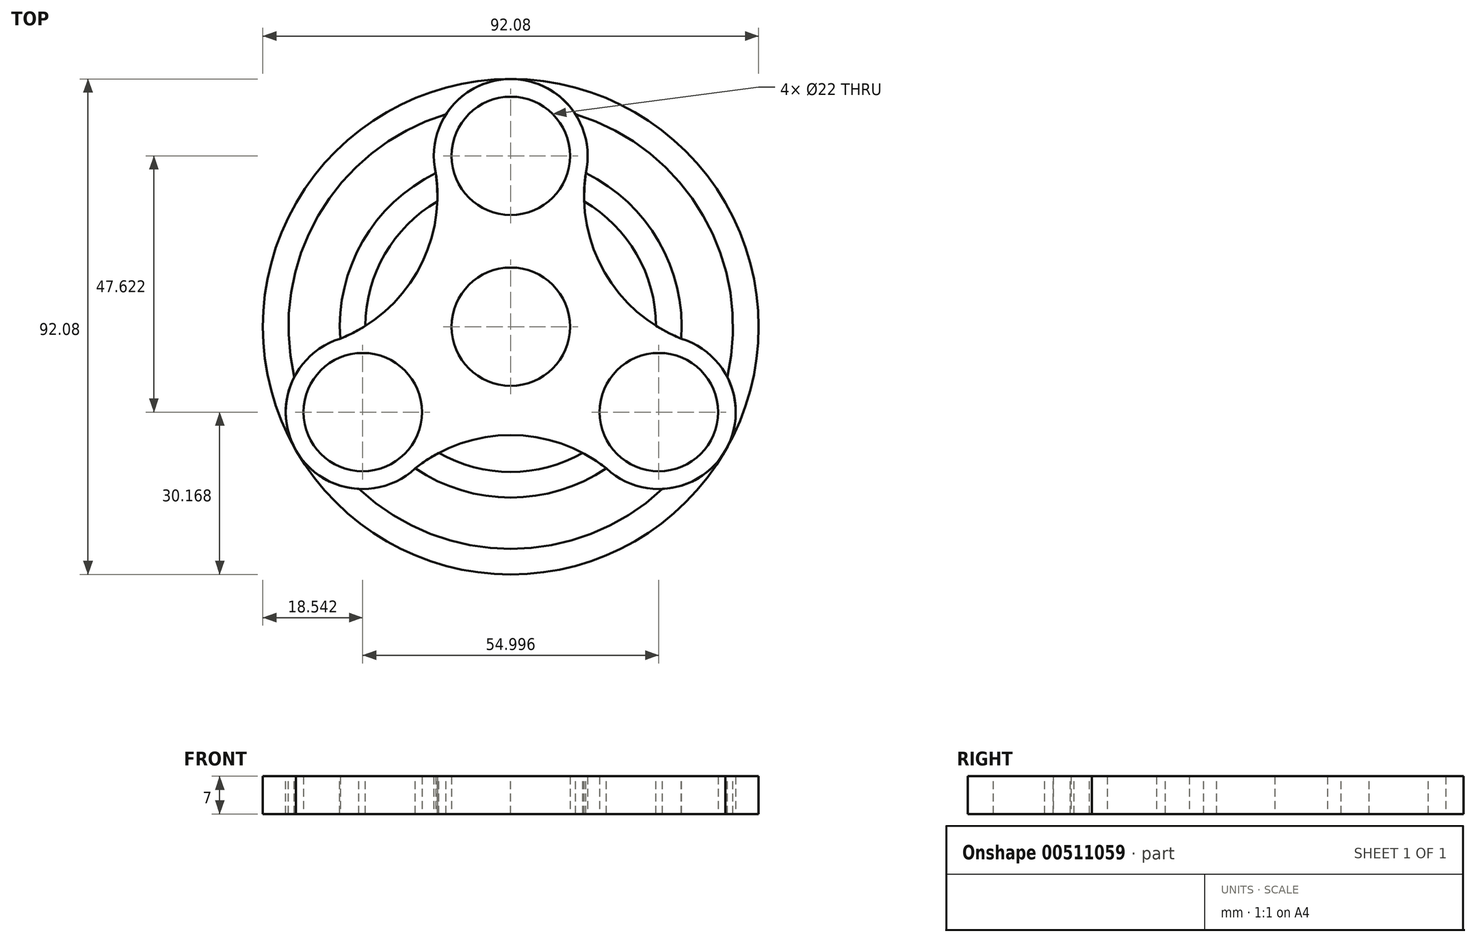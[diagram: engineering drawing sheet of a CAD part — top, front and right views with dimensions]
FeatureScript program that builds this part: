
annotation { "Feature Type Name" : "Feature", "Feature Type Description" : "" }
export const myFeature = defineFeature(function(context is Context, id is Id, definition is map)
    precondition{}
    {
        {
            var Q0;
            Q0=qCreatedBy(makeId("Top.planeOp"),FACE);
            var sketch = newSketch(context, id + "F0", { "sketchPlane" : qUnion([Q0])});
            skArc(sketch, "E0", {"start": v(-31.67, -2.2) * mm, "mid": v(-27.5, -15.87) * mm, "end": v(-17.75, -26.32) * mm});
            skCircle(sketch, "E1", {"center": v(0, 31.75) * mm, "radius": 14.29 * mm});
            skCircle(sketch, "E2", {"center": v(27.5, -15.87) * mm, "radius": 14.29 * mm});
            skCircle(sketch, "E3", {"center": v(-27.5, -15.87) * mm, "radius": 14.29 * mm});
            skArc(sketch, "E4", {"start": v(-31.67, -2.2) * mm, "mid": v(-17.44, 10.07) * mm, "end": v(-13.92, 28.54) * mm});
            skArc(sketch, "E5", {"start": v(13.92, 28.54) * mm, "mid": v(17.44, 10.07) * mm, "end": v(31.67, -2.2) * mm});
            skArc(sketch, "E6", {"start": v(17.75, -26.32) * mm, "mid": v(0, -20.14) * mm, "end": v(-17.75, -26.32) * mm});
            skArc(sketch, "E7.trimOffspring", {"start": v(13.92, 28.54) * mm, "mid": v(0, 31.75) * mm, "end": v(-13.92, 28.54) * mm});
            skArc(sketch, "E8.trimOffspring", {"start": v(17.75, -26.32) * mm, "mid": v(27.5, -15.87) * mm, "end": v(31.67, -2.2) * mm});
            skCircle(sketch, "E9", {"center": v(0, 31.75) * mm, "radius": 11 * mm});
            skCircle(sketch, "E10", {"center": v(-27.5, -15.87) * mm, "radius": 11 * mm});
            skCircle(sketch, "E11", {"center": v(27.5, -15.87) * mm, "radius": 11 * mm});
            skCircle(sketch, "E12", {"center": v(0, 0) * mm, "radius": 11 * mm});
            skSolve(sketch);
        }
        {
            var Q0;
            {var subQ0=sQuery(id+"F0.wireOp",EDGE,"E7.trimOffspring");var subQ4=sQuery(id+"F0.wireOp",EDGE,"E9");var subQ6=makeQuery(id+"F0.imprint","INTERSECT",VERTEX,{"disambiguationData":[OD(0.0)],"derivedFrom":[subQ0,subQ4]});Q0=makeQuery(id+"F0.imprint","IMPRINT",FACE,{"disambiguationData":[TD([[makeQuery(id+"F0.imprint","IMPRINT",EDGE,{"disambiguationData":[TD([[subQ6,-1.0]])],"derivedFrom":subQ4}),-1.0]])]});}
            var Q1;
            {var subQ0=sQuery(id+"F0.wireOp",EDGE,"E7.trimOffspring");var subQ4=sQuery(id+"F0.wireOp",EDGE,"E9");var subQ5=makeQuery(id+"F0.imprint","INTERSECT",VERTEX,{"disambiguationData":[OD(0.0)],"derivedFrom":[subQ0,subQ4]});Q1=makeQuery(id+"F0.imprint","IMPRINT",FACE,{"disambiguationData":[TD([[makeQuery(id+"F0.imprint","IMPRINT",EDGE,{"disambiguationData":[TD([[subQ5,1.0]])],"derivedFrom":subQ4}),-1.0]])]});}
            var Q2;
            {var subQ0=sQuery(id+"F0.wireOp",EDGE,"E4");Q2=makeQuery(id+"F0.imprint","IMPRINT",FACE,{"disambiguationData":[TD([[makeQuery(id+"F0.imprint","IMPRINT",EDGE,{"derivedFrom":subQ0}),-1.0]])]});}
            var Q3;
            {var subQ0=sQuery(id+"F0.wireOp",EDGE,"E8.trimOffspring");var subQ4=sQuery(id+"F0.wireOp",EDGE,"E11");var subQ5=makeQuery(id+"F0.imprint","INTERSECT",VERTEX,{"disambiguationData":[OD(0.0)],"derivedFrom":[subQ0,subQ4]});Q3=makeQuery(id+"F0.imprint","IMPRINT",FACE,{"disambiguationData":[TD([[makeQuery(id+"F0.imprint","IMPRINT",EDGE,{"disambiguationData":[TD([[subQ5,1.0]])],"derivedFrom":subQ4}),-1.0]])]});}
            var Q4;
            {var subQ0=sQuery(id+"F0.wireOp",EDGE,"E8.trimOffspring");var subQ4=sQuery(id+"F0.wireOp",EDGE,"E11");var subQ5=makeQuery(id+"F0.imprint","INTERSECT",VERTEX,{"disambiguationData":[OD(0.0)],"derivedFrom":[subQ0,subQ4]});Q4=makeQuery(id+"F0.imprint","IMPRINT",FACE,{"disambiguationData":[TD([[makeQuery(id+"F0.imprint","IMPRINT",EDGE,{"disambiguationData":[TD([[subQ5,-1.0]])],"derivedFrom":subQ4}),-1.0]])]});}
            var Q5;
            {var subQ1=sQuery(id+"F0.wireOp",EDGE,"E0");var subQ3=sQuery(id+"F0.wireOp",EDGE,"E10");var subQ4=makeQuery(id+"F0.imprint","INTERSECT",VERTEX,{"disambiguationData":[OD(0.0)],"derivedFrom":[subQ1,subQ3]});Q5=makeQuery(id+"F0.imprint","IMPRINT",FACE,{"disambiguationData":[TD([[makeQuery(id+"F0.imprint","IMPRINT",EDGE,{"disambiguationData":[TD([[subQ4,1.0]])],"derivedFrom":subQ3}),-1.0]])]});}
            var Q6;
            {var subQ1=sQuery(id+"F0.wireOp",EDGE,"E0");var subQ3=sQuery(id+"F0.wireOp",EDGE,"E10");var subQ4=makeQuery(id+"F0.imprint","INTERSECT",VERTEX,{"disambiguationData":[OD(0.0)],"derivedFrom":[subQ1,subQ3]});Q6=makeQuery(id+"F0.imprint","IMPRINT",FACE,{"disambiguationData":[TD([[makeQuery(id+"F0.imprint","IMPRINT",EDGE,{"disambiguationData":[TD([[subQ4,-1.0]])],"derivedFrom":subQ3}),-1.0]])]});}
            extrude(context, id + "F1", {"entities" : qUnion([Q0, Q1, Q2, Q3, Q4, Q5, Q6]), "depth" : 7 * mm});
        }
        {
            var Q0;
            Q0=makeQuery(id+"F1.opExtrude","CAP_FACE",FACE,{"disambiguationData":[OSD([sQuery(id+"F0.wireOp",EDGE,"E1"),sQuery(id+"F0.wireOp",EDGE,"E2"),sQuery(id+"F0.wireOp",EDGE,"E3"),sQuery(id+"F0.wireOp",EDGE,"E4"),sQuery(id+"F0.wireOp",EDGE,"E5"),sQuery(id+"F0.wireOp",EDGE,"E6"),sQuery(id+"F0.wireOp",EDGE,"E9"),sQuery(id+"F0.wireOp",EDGE,"E10"),sQuery(id+"F0.wireOp",EDGE,"E11"),sQuery(id+"F0.wireOp",EDGE,"E12")])],"isStart":false});
            var sketch = newSketch(context, id + "F2", { "sketchPlane" : qUnion([Q0])});
            skCircle(sketch, "E13", {"center": v(0, 0) * mm, "radius": 46.04 * mm});
            skArc(sketch, "E14", {"start": v(-12, 39.49) * mm, "mid": v(-35.74, 20.64) * mm, "end": v(-40.2, -9.34) * mm});
            skArc(sketch, "E15", {"start": v(-13.63, 23.29) * mm, "mid": v(-23.37, 13.5) * mm, "end": v(-26.99, 0.17) * mm});
            skArc(sketch, "E16.0", {"start": v(13.92, 28.54) * mm, "mid": v(0, 46.04) * mm, "end": v(-13.92, 28.54) * mm});
            skArc(sketch, "E17.0", {"start": v(-31.67, -2.2) * mm, "mid": v(-17.44, 10.07) * mm, "end": v(-13.92, 28.54) * mm});
            skArc(sketch, "E18.0", {"start": v(13.92, 28.54) * mm, "mid": v(17.44, 10.07) * mm, "end": v(31.67, -2.2) * mm});
            skArc(sketch, "E19.0", {"start": v(17.75, -26.32) * mm, "mid": v(39.87, -23.01) * mm, "end": v(31.67, -2.2) * mm});
            skArc(sketch, "E20.0", {"start": v(17.75, -26.32) * mm, "mid": v(0, -20.14) * mm, "end": v(-17.75, -26.32) * mm});
            skArc(sketch, "E21.0", {"start": v(-31.67, -2.2) * mm, "mid": v(-39.87, -23.01) * mm, "end": v(-17.75, -26.32) * mm});
            skArc(sketch, "E22.trimOffspring", {"start": v(26.99, 0.17) * mm, "mid": v(23.37, 13.5) * mm, "end": v(13.63, 23.29) * mm});
            skArc(sketch, "E23.trimOffspring", {"start": v(-13.36, -23.45) * mm, "mid": v(0, -26.99) * mm, "end": v(13.36, -23.45) * mm});
            skArc(sketch, "E24.trimOffspring", {"start": v(-28.2, -30.14) * mm, "mid": v(0, -41.28) * mm, "end": v(28.2, -30.14) * mm});
            skArc(sketch, "E25.trimOffspring", {"start": v(40.2, -9.34) * mm, "mid": v(35.74, 20.64) * mm, "end": v(12, 39.49) * mm});
            skArc(sketch, "E26", {"start": v(-13.92, 28.54) * mm, "mid": v(-27.5, 15.88) * mm, "end": v(-31.67, -2.2) * mm});
            skArc(sketch, "E27.trimOffspring", {"start": v(31.67, -2.2) * mm, "mid": v(27.5, 15.88) * mm, "end": v(13.92, 28.54) * mm});
            skArc(sketch, "E28.trimOffspring", {"start": v(-17.75, -26.32) * mm, "mid": v(0, -31.75) * mm, "end": v(17.75, -26.32) * mm});
            skSolve(sketch);
        }
        {
            var Q0;
            {var subQ5=sQuery(id+"F2.wireOp",EDGE,"E14");Q0=makeQuery(id+"F2.imprint","IMPRINT",FACE,{"disambiguationData":[TD([[makeQuery(id+"F2.imprint","IMPRINT",EDGE,{"derivedFrom":subQ5}),-1.0]])]});}
            var Q1;
            {var subQ5=sQuery(id+"F2.wireOp",EDGE,"E25.trimOffspring");Q1=makeQuery(id+"F2.imprint","IMPRINT",FACE,{"disambiguationData":[TD([[makeQuery(id+"F2.imprint","IMPRINT",EDGE,{"derivedFrom":subQ5}),-1.0]])]});}
            var Q2;
            {var subQ2=sQuery(id+"F2.wireOp",EDGE,"E22.trimOffspring");Q2=makeQuery(id+"F2.imprint","IMPRINT",FACE,{"disambiguationData":[TD([[makeQuery(id+"F2.imprint","IMPRINT",EDGE,{"derivedFrom":subQ2}),-1.0]])]});}
            var Q3;
            {var subQ0=sQuery(id+"F2.wireOp",EDGE,"E15");Q3=makeQuery(id+"F2.imprint","IMPRINT",FACE,{"disambiguationData":[TD([[makeQuery(id+"F2.imprint","IMPRINT",EDGE,{"derivedFrom":subQ0}),-1.0]])]});}
            var Q4;
            {var subQ2=sQuery(id+"F2.wireOp",EDGE,"E23.trimOffspring");Q4=makeQuery(id+"F2.imprint","IMPRINT",FACE,{"disambiguationData":[TD([[makeQuery(id+"F2.imprint","IMPRINT",EDGE,{"derivedFrom":subQ2}),-1.0]])]});}
            var Q5;
            {var subQ5=sQuery(id+"F2.wireOp",EDGE,"E24.trimOffspring");Q5=makeQuery(id+"F2.imprint","IMPRINT",FACE,{"disambiguationData":[TD([[makeQuery(id+"F2.imprint","IMPRINT",EDGE,{"derivedFrom":subQ5}),-1.0]])]});}
            extrude(context, id + "F3", {"entities" : qUnion([Q0, Q1, Q2, Q3, Q4, Q5]), "oppositeDirection" : true, "depth" : 7 * mm});
        }
    });
